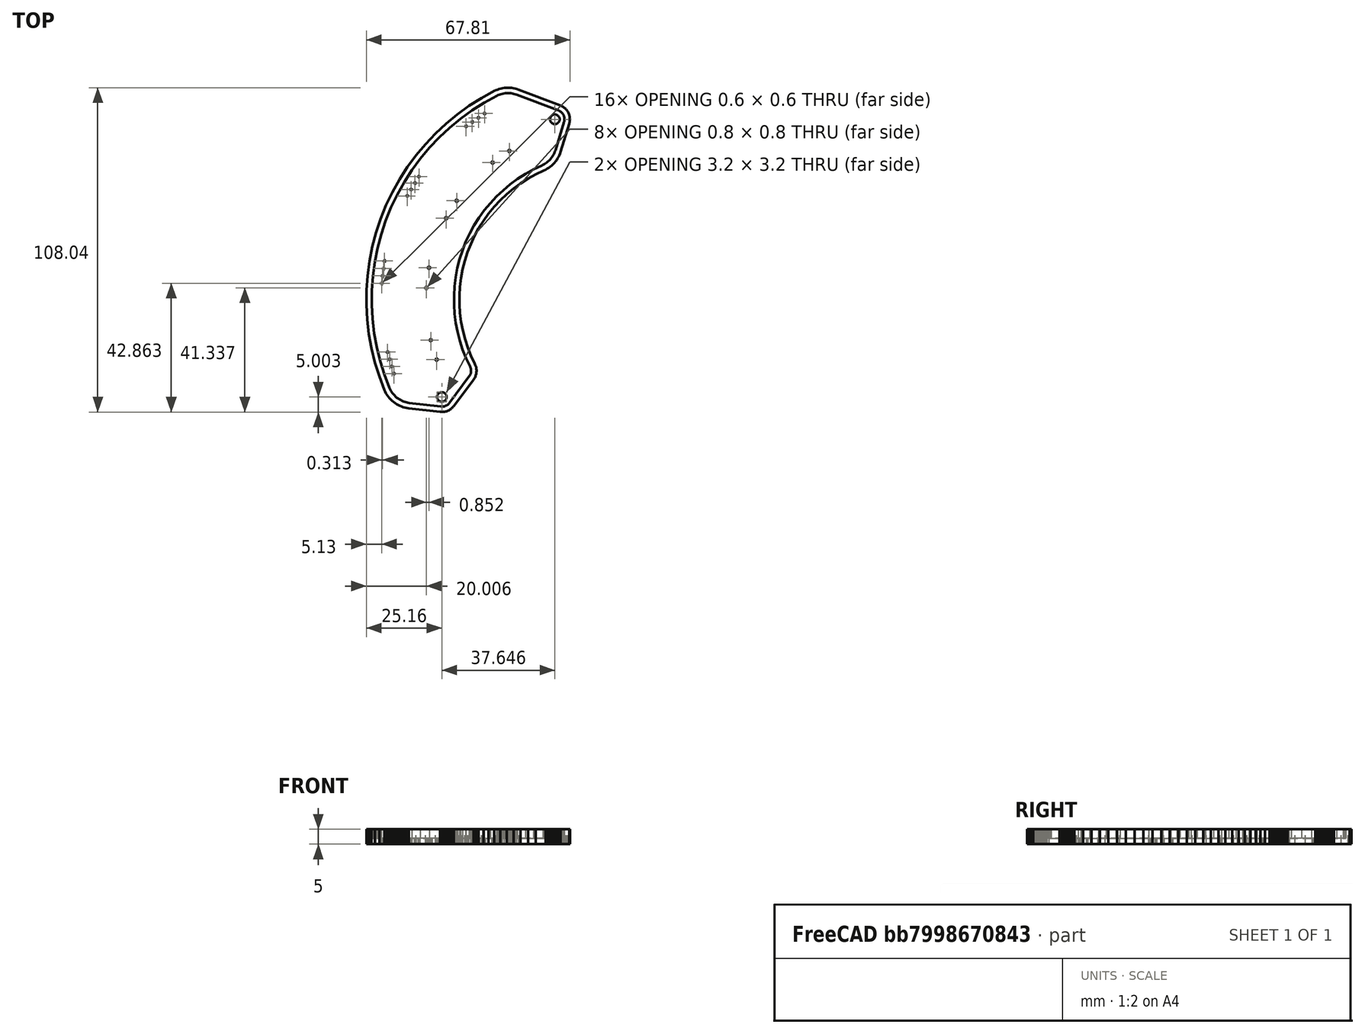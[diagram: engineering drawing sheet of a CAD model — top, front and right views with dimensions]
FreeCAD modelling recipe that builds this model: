
FCSTD DOCUMENT  (FreeCAD 1.0R39109 (Git))
Label: oledbase2
License: All rights reserved
LicenseURL: https://en.wikipedia.org/wiki/All_rights_reserved
objects: Part::Feature×1, Part::Refine×1, PartDesign::FeatureBase×1, PartDesign::Pad×1, Sketcher::SketchObject×1, PartDesign::Body×1
note: 10 computed .brp shape members not serialized (recipe doc carries the construction recipe); baked Part::Feature solids carry a one-line shape summary decoded from their .brp

FEATURE [Part::Feature] oledpart001_solid  label="oledpart001 (Solid)"
  shape: bbox 67.8 x 108 x 4 mm, 10964 faces (baked)
FEATURE [Part::Refine] oledpart001_solid001  label="oledpart001 (Solid)001"
  Source = -> oledpart001_solid
FEATURE [PartDesign::FeatureBase] BaseFeature
  BaseFeature = -> oledpart001_solid001
  Suppressed = false
FEATURE [PartDesign::Pad] Pad
  BaseFeature = -> BaseFeature
  Direction = (0,0,1)
  Length = 1
  Length2 = 10
  Profile = -> BaseFeature [Face1]
  Refine = true
  Suppressed = false
  Type = 0
FEATURE [Sketcher::SketchObject] Sketch
  ArcFitTolerance = 1e-06
  AttachmentSupport = -> [Pad]
  FullyConstrained = true
  MakeInternals = false
  MapMode = 5
  Placement = pos=(0,0,2) rot=(0,0,1;0rad)
FEATURE [PartDesign::Body] Body
  AllowCompound = false
  BaseFeature = -> oledpart001_solid001
  Group = -> [BaseFeature,Pad,Sketch]
  Origin = -> Origin
  Tip = -> Pad
